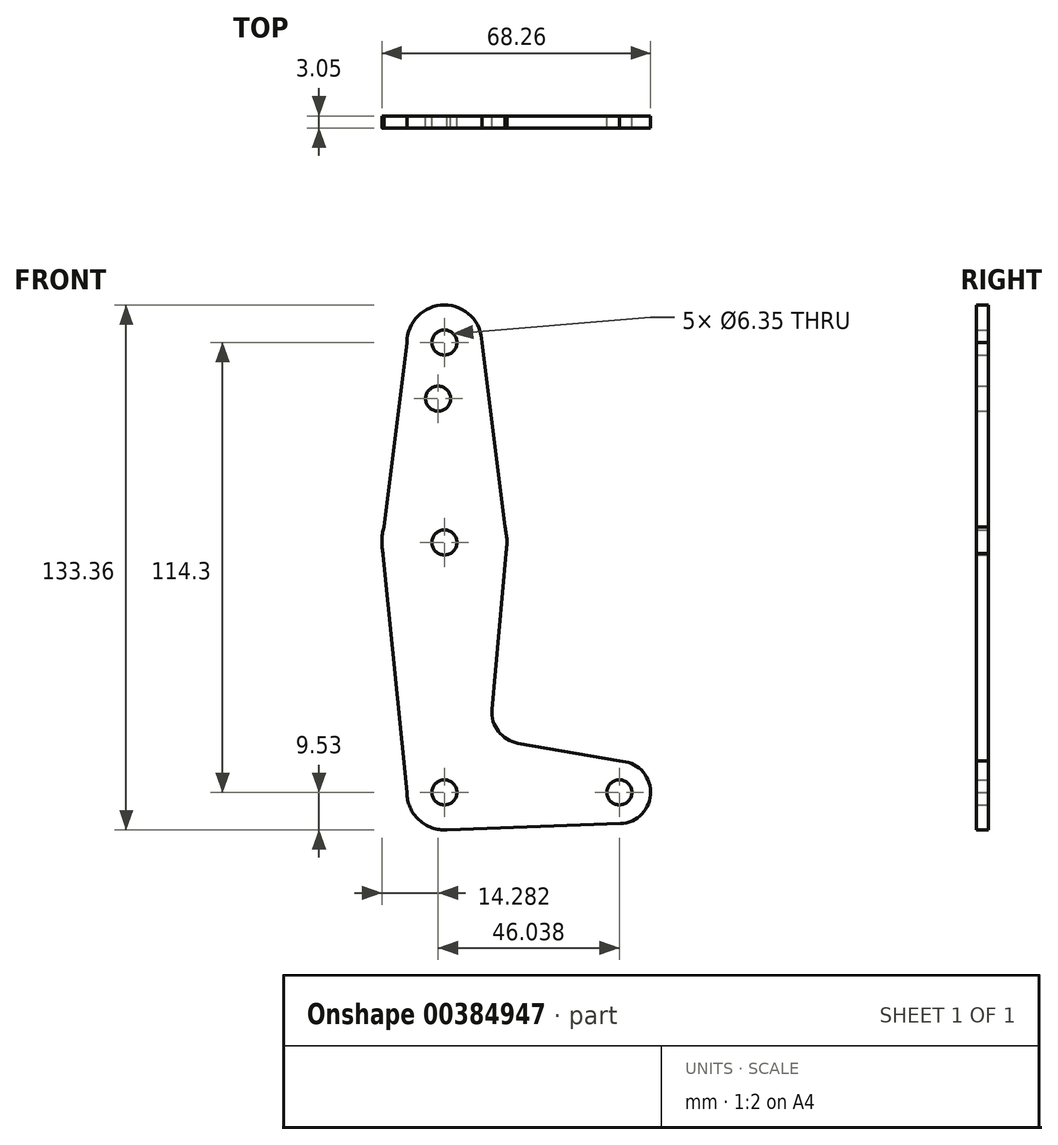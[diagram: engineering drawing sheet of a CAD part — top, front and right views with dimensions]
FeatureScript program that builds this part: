
annotation { "Feature Type Name" : "Feature", "Feature Type Description" : "" }
export const myFeature = defineFeature(function(context is Context, id is Id, definition is map)
    precondition{}
    {
        {
            var Q0;
            Q0=qCreatedBy(makeId("Front.planeOp"),FACE);
            var sketch = newSketch(context, id + "F0", { "sketchPlane" : qUnion([Q0])});
            skCircle(sketch, "E0", {"center": v(0, 0) * mm, "radius": 9.53 * mm});
            skLineSegment(sketch, "E1", {"start": v(0, 0) * mm, "end": v(0, 114.3) * mm, "construction": true});
            skCircle(sketch, "E2", {"center": v(0, 114.3) * mm, "radius": 9.53 * mm});
            skLineSegment(sketch, "E3", {"start": v(0, 0) * mm, "end": v(44.45, 0) * mm, "construction": true});
            skCircle(sketch, "E4", {"center": v(44.45, 0) * mm, "radius": 7.94 * mm});
            skCircle(sketch, "E5", {"center": v(0, 63.5) * mm, "radius": 15.88 * mm});
            skLineSegment(sketch, "E6", {"start": v(0, -9.53) * mm, "end": v(44.73, -7.93) * mm});
            skCircle(sketch, "E7", {"center": v(0, 114.3) * mm, "radius": 3.18 * mm});
            skCircle(sketch, "E8", {"center": v(0, 63.5) * mm, "radius": 3.18 * mm});
            skCircle(sketch, "E9", {"center": v(0, 0) * mm, "radius": 3.18 * mm});
            skCircle(sketch, "E10", {"center": v(44.45, 0) * mm, "radius": 3.18 * mm});
            skCircle(sketch, "E11", {"center": v(-1.59, 100.03) * mm, "radius": 3.18 * mm});
            skLineSegment(sketch, "E12", {"start": v(-15.88, 63.5) * mm, "end": v(-9.52, 114.3) * mm});
            skLineSegment(sketch, "E13", {"start": v(9.52, 114.3) * mm, "end": v(15.88, 63.5) * mm});
            skLineSegment(sketch, "E14", {"start": v(-15.88, 63.5) * mm, "end": v(-9.52, 0) * mm});
            skLineSegment(sketch, "E15", {"start": v(15.88, 63.5) * mm, "end": v(12.12, 21.02) * mm});
            skLineSegment(sketch, "E16", {"start": v(18.65, 12.5) * mm, "end": v(44.45, 7.94) * mm});
            skPoint(sketch, "E17.newPointB", {"position": v(10.26, 0) * mm});
            skArc(sketch, "E17.filletArc", {"start": v(12.12, 21.02) * mm, "mid": v(13.73, 15.48) * mm, "end": v(18.65, 12.5) * mm});
            skSolve(sketch);
        }
        {
            var Q0;
            Q0 = qSketchRegion(id + "F0", true);
            extrude(context, id + "F1", {"entities" : qUnion([Q0]), "depth" : 3.05 * mm});
        }
    });
